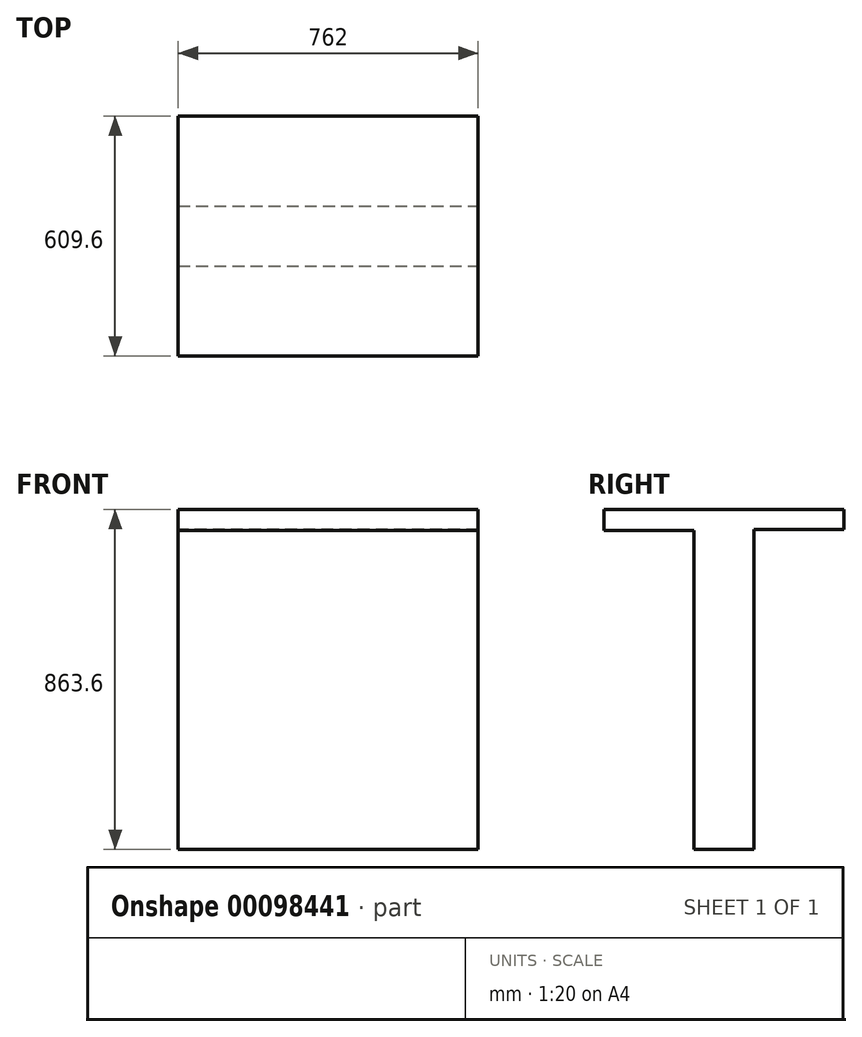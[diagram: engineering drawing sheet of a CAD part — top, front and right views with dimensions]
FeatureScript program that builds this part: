
annotation { "Feature Type Name" : "Feature", "Feature Type Description" : "" }
export const myFeature = defineFeature(function(context is Context, id is Id, definition is map)
    precondition{}
    {
        {
            var Q0;
            Q0=qCreatedBy(makeId("Top.planeOp"),FACE);
            var sketch = newSketch(context, id + "F0", { "sketchPlane" : qUnion([Q0])});
            skLineSegment(sketch, "E0.bottom", {"start": v(-580.58, -484.28) * mm, "end": v(181.42, -484.28) * mm});
            skLineSegment(sketch, "E0.top", {"start": v(-580.58, 125.32) * mm, "end": v(181.42, 125.32) * mm});
            skLineSegment(sketch, "E0.left", {"start": v(-580.58, -484.28) * mm, "end": v(-580.58, 125.32) * mm});
            skLineSegment(sketch, "E0.right", {"start": v(181.42, -484.28) * mm, "end": v(181.42, 125.32) * mm});
            skSolve(sketch);
        }
        {
            var Q0;
            Q0 = qSketchRegion(id + "F0", true);
            extrude(context, id + "F1", {"entities" : qUnion([Q0]), "depth" : 863.6 * mm});
        }
        {
            var Q0;
            Q0=makeQuery(id+"F1.opExtrude","SWEPT_FACE",FACE,{"disambiguationData":[OSD([sQuery(id+"F0.wireOp",EDGE,"E0.bottom")])]});
            var sketch = newSketch(context, id + "F2", { "sketchPlane" : qUnion([Q0])});
            skLineSegment(sketch, "E1.bottom", {"start": v(-580.58, 0) * mm, "end": v(181.42, 0) * mm});
            skLineSegment(sketch, "E1.top", {"start": v(-580.58, 810.15) * mm, "end": v(181.42, 810.15) * mm});
            skLineSegment(sketch, "E1.left", {"start": v(-580.58, 0) * mm, "end": v(-580.58, 810.15) * mm});
            skLineSegment(sketch, "E1.right", {"start": v(181.42, 0) * mm, "end": v(181.42, 810.15) * mm});
            skSolve(sketch);
        }
        {
            var Q0;
            Q0 = qSketchRegion(id + "F2", true);
            extrude(context, id + "F3", {"entities" : qUnion([Q0]), "operationType" : NewBodyOperationType.REMOVE, "oppositeDirection" : true, "depth" : 228.6 * mm});
        }
        {
            var Q0;
            Q0=makeQuery(id+"F1.opExtrude","SWEPT_FACE",FACE,{"disambiguationData":[OSD([sQuery(id+"F0.wireOp",EDGE,"E0.top")])]});
            var sketch = newSketch(context, id + "F4", { "sketchPlane" : qUnion([Q0])});
            skLineSegment(sketch, "E2.bottom", {"start": v(-181.42, 812.8) * mm, "end": v(580.58, 812.8) * mm});
            skLineSegment(sketch, "E2.top", {"start": v(-181.42, 0) * mm, "end": v(580.58, 0) * mm});
            skLineSegment(sketch, "E2.left", {"start": v(-181.42, 812.8) * mm, "end": v(-181.42, 0) * mm});
            skLineSegment(sketch, "E2.right", {"start": v(580.58, 812.8) * mm, "end": v(580.58, 0) * mm});
            skSolve(sketch);
        }
        {
            var Q0;
            Q0 = qSketchRegion(id + "F4", true);
            extrude(context, id + "F5", {"entities" : qUnion([Q0]), "operationType" : NewBodyOperationType.REMOVE, "oppositeDirection" : true, "depth" : 228.6 * mm});
        }
    });
